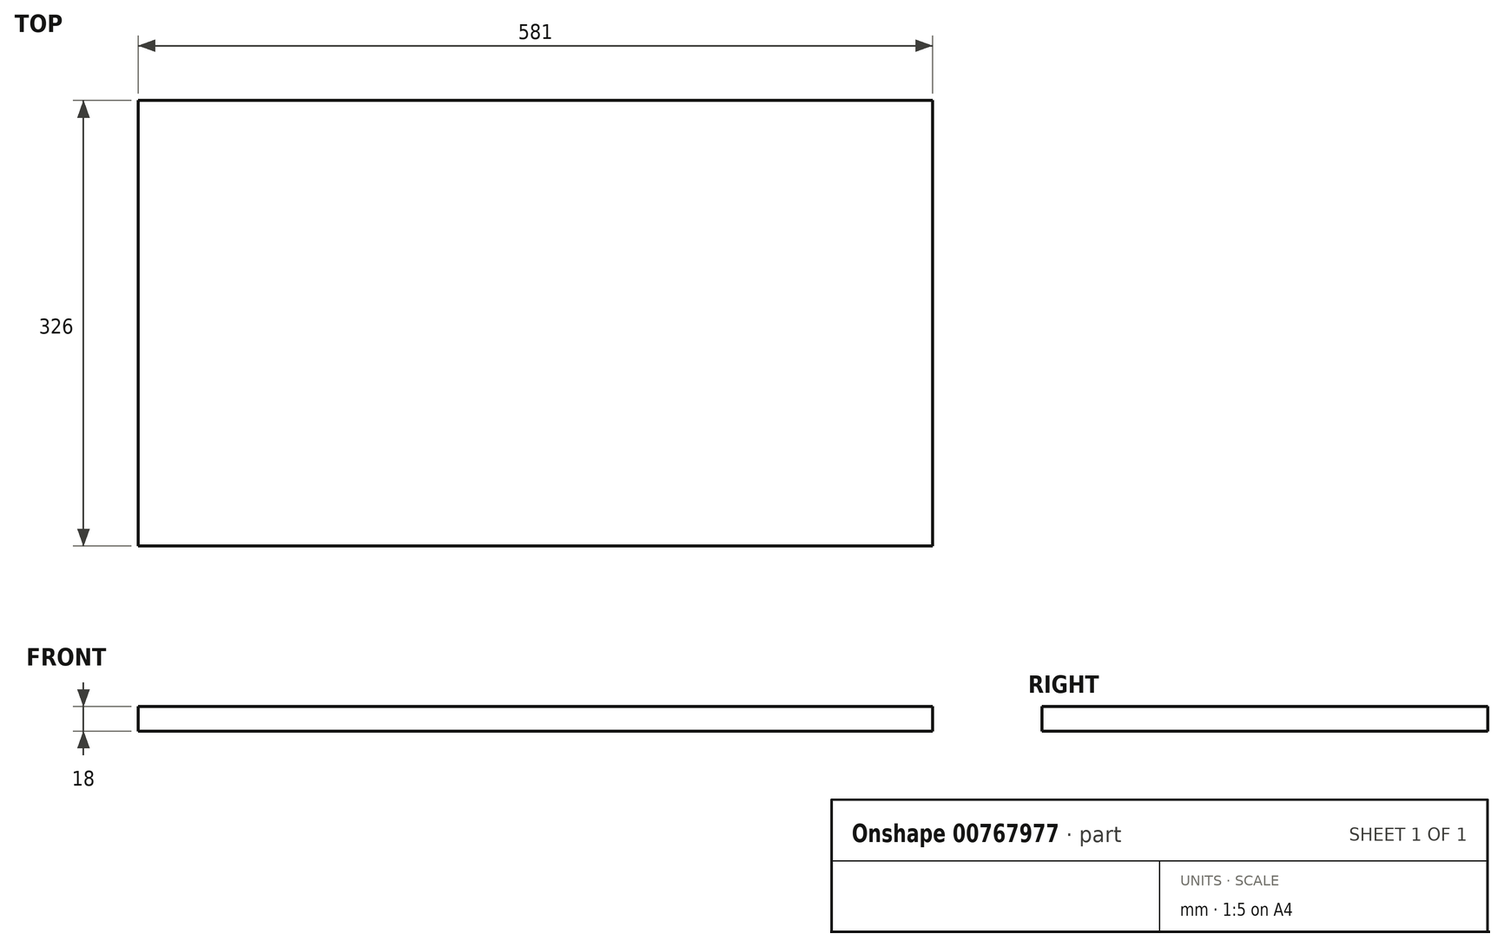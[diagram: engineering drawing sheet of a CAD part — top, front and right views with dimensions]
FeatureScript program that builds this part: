
annotation { "Feature Type Name" : "Feature", "Feature Type Description" : "" }
export const myFeature = defineFeature(function(context is Context, id is Id, definition is map)
    precondition{}
    {
        {
            var Q0;
            Q0=qCreatedBy(makeId("Top.planeOp"),FACE);
            var sketch = newSketch(context, id + "F0", { "sketchPlane" : qUnion([Q0])});
            skLineSegment(sketch, "E0.bottom", {"start": v(-290.5, 163) * mm, "end": v(290.5, 163) * mm});
            skLineSegment(sketch, "E0.top", {"start": v(-290.5, -163) * mm, "end": v(290.5, -163) * mm});
            skLineSegment(sketch, "E0.left", {"start": v(-290.5, 163) * mm, "end": v(-290.5, -163) * mm});
            skLineSegment(sketch, "E0.right", {"start": v(290.5, 163) * mm, "end": v(290.5, -163) * mm});
            skPoint(sketch, "E0.middle", {"position": v(0, 0) * mm});
            skSolve(sketch);
        }
        {
            var Q0;
            Q0 = qSketchRegion(id + "F0", true);
            extrude(context, id + "F1", {"entities" : qUnion([Q0]), "depth" : 18 * mm, "offsetDistance" : 25 * mm});
        }
    });
